# Revit family: REVIT-TR-125-215
name_source: partatom
category: Mechanical Equipment
revit_build: Autodesk Revit 2017 (Build: 20190507_1515(x64)
units: mm (PartAtom-declared; Revit-internal decimal feet)

## family parameters
Always vertical = Yes
Cut with Voids When Loaded = No
Part Type = Normal
Room Calculation Point = No
Round Connector Dimension = Use Radius
Shared = No
Work Plane-Based = No

## types (4) — shared parameters
Assembly Code = D3040400
Cold Inlet NPT = 2"
Cold Inlet Radius = 1"
Description = Storage Tanks for Hot Water
Disclaimer = This rendering is for building modeling purposes only. Submittal/catalog is still the contract document. PVI reserves the right to change design and specification without notice.
Drain Angle = 90.00°
Drain Height = 3 1/2"
Drain NPT = 1"
Drain Radius = 1/2"
From Heater NPT = 2"
From Heater Radius = 1"
Hot Outlet NPT = 2"
Hot Outlet Radius = 1"
Manufacturer = PVI Industries, LLC
Manway Access Extension = 1"
Manway Access Radius = 6 1/2"
Relief NPT = 1"
Relief Radius = 1/2"
To Heater NPT = 2"
To Heater Radius = 1"
URL = www.pvi.com

## per-type parameters (varying)
| type | Cold Inlet Extension | Cold Inlet Height | Controll Access Angle | Drain Extension | Flat Side Distance | From Heater Extension | From Heater Height | Gallons Storage | Height to Upper Drain | Relief Angle | Relief Extension | Relief Height | Skid Length | Skid Spacing | SkidWidthBetweenCenters | To Heater Extension | To Heater Height | Unit Diameter | Unit Height | Unit Radius | Weight |
| L 125A-TR | 15 3/4" | 15" | 50.70° | 18 5/8" | 29 127/256" | 15 3/4" | 15" | 125 CF | 25 9/64" | 62.00° | 15 3/4" | 64 1/8" | 30" | 16" | 20" | 15 3/4" | 23" | 29 1/2" | 75" | 14 3/4" | 755 |
| L 150A-TR | 19 1/2" | 15 3/4" | 45.00° | 22 3/8" | 34" | 19 1/2" | 19" | 150 CF | 20" | 38.00° | 19 1/2" | 53 1/4" | 37" | 17" | 21" | 19 1/2" | 27" | 37" | 65" | 18 1/2" | 815 |
| L 175A-TR | 19 1/2" | 15 3/4" | 45.00° | 22 3/8" | 34" | 19 1/2" | 19" | 175 CF | 25 9/64" | 38.00° | 19 1/2" | 59 5/16" | 37" | 17" | 21" | 19 1/2" | 27" | 37" | 71" | 18 1/2" | 855 |
| L 215A-TR | 19 1/2" | 15 3/4" | 45.00° | 22 3/8" | 34" | 19 1/2" | 19" | 215 CF | 25 9/64" | 38.00° | 19 1/2" | 65 7/8" | 37" | 17" | 21" | 19 1/2" | 27" | 37" | 78" | 18 1/2" | 895 |

note: column(s) folded — value = type name in every type: Model

## geometry (parser evidence)
native form markers: Sweep x2
no freeform markers — native parametric forms only
